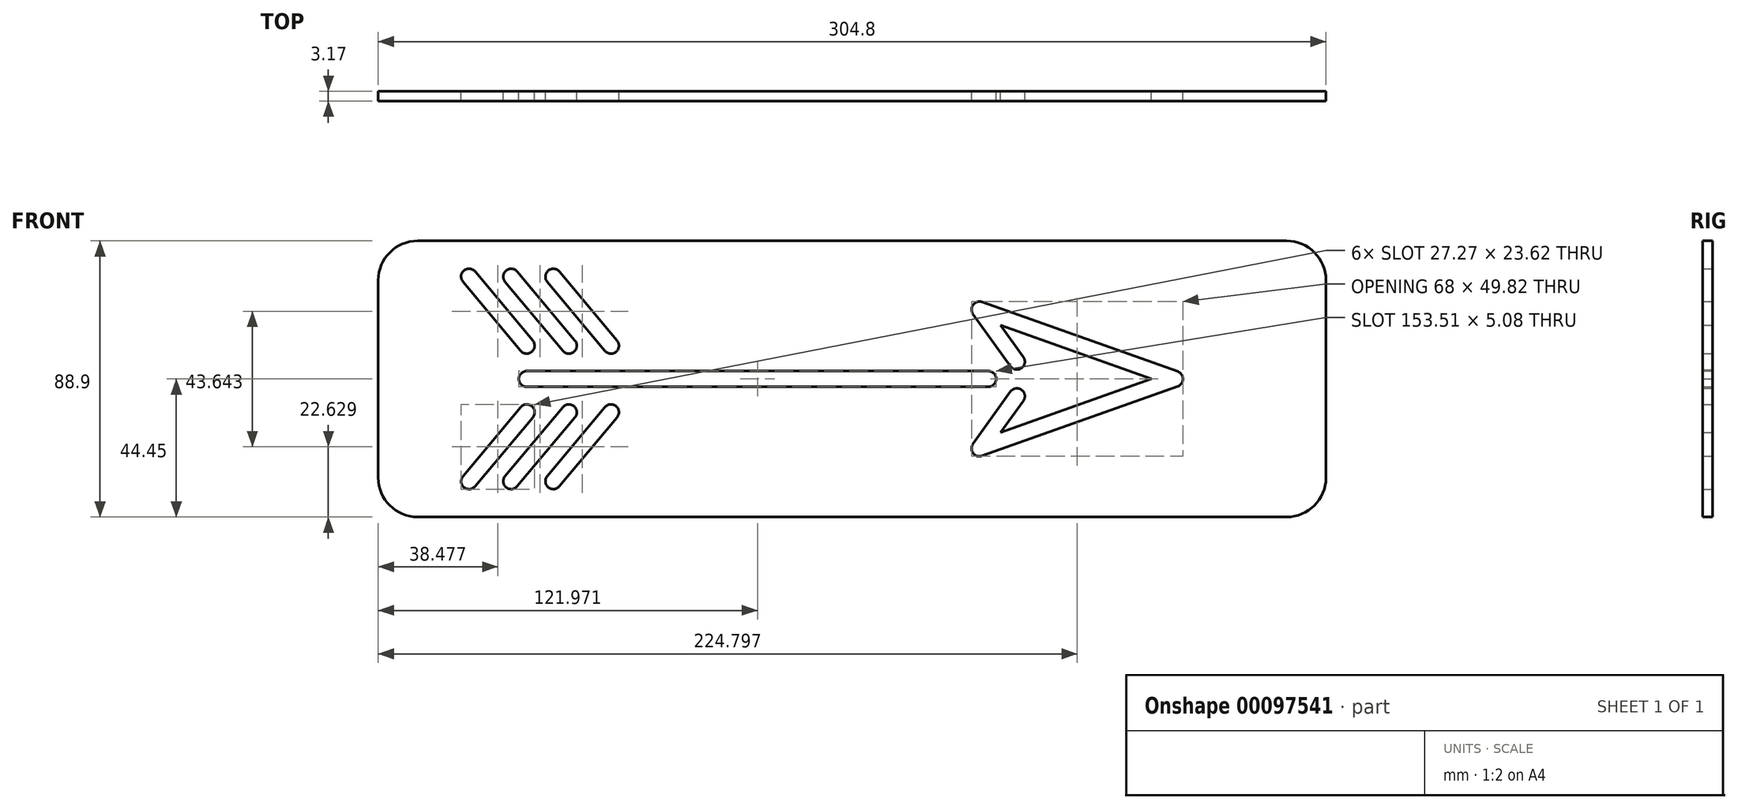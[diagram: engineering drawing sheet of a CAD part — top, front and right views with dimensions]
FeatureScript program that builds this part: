
annotation { "Feature Type Name" : "Feature", "Feature Type Description" : "" }
export const myFeature = defineFeature(function(context is Context, id is Id, definition is map)
    precondition{}
    {
        {
            var Q0;
            Q0=qCreatedBy(makeId("Front.planeOp"),FACE);
            var sketch = newSketch(context, id + "F0", { "sketchPlane" : qUnion([Q0])});
            skLineSegment(sketch, "E0.bottom", {"start": v(-139.7, -44.45) * mm, "end": v(139.7, -44.45) * mm});
            skLineSegment(sketch, "E0.top", {"start": v(-139.7, 44.45) * mm, "end": v(139.7, 44.45) * mm});
            skLineSegment(sketch, "E0.left", {"start": v(-152.4, -31.75) * mm, "end": v(-152.4, 31.75) * mm});
            skLineSegment(sketch, "E0.right", {"start": v(152.4, -31.75) * mm, "end": v(152.4, 31.75) * mm});
            skPoint(sketch, "E0.middle", {"position": v(0, 0) * mm});
            skArc(sketch, "E1.1.startCap", {"start": v(-75.59, 12.34) * mm, "mid": v(-75.91, 8.77) * mm, "end": v(-79.49, 9.09) * mm});
            skArc(sketch, "E1.1.endCap", {"start": v(-98.05, 31.3) * mm, "mid": v(-97.73, 34.88) * mm, "end": v(-94.15, 34.56) * mm});
            skLineSegment(sketch, "E1.1.left", {"start": v(-79.49, 9.09) * mm, "end": v(-98.05, 31.3) * mm});
            skLineSegment(sketch, "E1.1.right", {"start": v(-75.59, 12.34) * mm, "end": v(-94.15, 34.56) * mm});
            skArc(sketch, "E1.2.startCap", {"start": v(-89.14, 12.34) * mm, "mid": v(-89.46, 8.77) * mm, "end": v(-93.04, 9.09) * mm});
            skArc(sketch, "E1.2.endCap", {"start": v(-111.6, 31.3) * mm, "mid": v(-111.28, 34.88) * mm, "end": v(-107.7, 34.56) * mm});
            skLineSegment(sketch, "E1.2.left", {"start": v(-93.04, 9.09) * mm, "end": v(-111.6, 31.3) * mm});
            skLineSegment(sketch, "E1.2.right", {"start": v(-89.14, 12.34) * mm, "end": v(-107.7, 34.56) * mm});
            skArc(sketch, "E1.3.startCap", {"start": v(-102.7, 12.34) * mm, "mid": v(-103.01, 8.77) * mm, "end": v(-106.6, 9.09) * mm});
            skArc(sketch, "E1.3.endCap", {"start": v(-125.15, 31.3) * mm, "mid": v(-124.83, 34.88) * mm, "end": v(-121.26, 34.56) * mm});
            skLineSegment(sketch, "E1.3.left", {"start": v(-106.6, 9.09) * mm, "end": v(-125.15, 31.3) * mm});
            skLineSegment(sketch, "E1.3.right", {"start": v(-102.7, 12.34) * mm, "end": v(-121.26, 34.56) * mm});
            skArc(sketch, "E2.0.startCap", {"start": v(-104.64, -2.54) * mm, "mid": v(-107.18, 0) * mm, "end": v(-104.64, 2.54) * mm});
            skArc(sketch, "E2.0.endCap", {"start": v(43.78, 2.54) * mm, "mid": v(46.32, 0) * mm, "end": v(43.78, -2.54) * mm});
            skLineSegment(sketch, "E2.0.left", {"start": v(-104.64, 2.54) * mm, "end": v(43.78, 2.54) * mm});
            skLineSegment(sketch, "E2.0.right", {"start": v(-104.64, -2.54) * mm, "end": v(43.78, -2.54) * mm});
            skLineSegment(sketch, "E3", {"start": v(-104.64, 10.71) * mm, "end": v(-91.1, 10.71) * mm, "construction": true});
            skLineSegment(sketch, "E4", {"start": v(-91.1, 10.71) * mm, "end": v(-77.54, 10.71) * mm, "construction": true});
            skLineSegment(sketch, "E5", {"start": v(-77.54, 10.71) * mm, "end": v(-75, 10.71) * mm, "construction": true});
            skPoint(sketch, "E6.visualSharp", {"position": v(-152.4, 44.45) * mm});
            skArc(sketch, "E6.filletArc", {"start": v(-139.7, 44.45) * mm, "mid": v(-148.68, 40.73) * mm, "end": v(-152.4, 31.75) * mm});
            skPoint(sketch, "E7.visualSharp", {"position": v(-152.4, -44.45) * mm});
            skArc(sketch, "E7.filletArc", {"start": v(-152.4, -31.75) * mm, "mid": v(-148.68, -40.73) * mm, "end": v(-139.7, -44.45) * mm});
            skPoint(sketch, "E8.visualSharp", {"position": v(152.4, 44.45) * mm});
            skArc(sketch, "E8.filletArc", {"start": v(152.4, 31.75) * mm, "mid": v(148.68, 40.73) * mm, "end": v(139.7, 44.45) * mm});
            skPoint(sketch, "E9.visualSharp", {"position": v(152.4, -44.45) * mm});
            skArc(sketch, "E9.filletArc", {"start": v(139.7, -44.45) * mm, "mid": v(148.68, -40.73) * mm, "end": v(152.4, -31.75) * mm});
            skArc(sketch, "E10.MirrorCS", {"start": v(-75.59, -12.34) * mm, "mid": v(-75.91, -8.77) * mm, "end": v(-79.49, -9.09) * mm});
            skArc(sketch, "E11.MirrorCS", {"start": v(-89.14, -12.34) * mm, "mid": v(-89.46, -8.77) * mm, "end": v(-93.04, -9.09) * mm});
            skArc(sketch, "E12.MirrorCS", {"start": v(-102.7, -12.34) * mm, "mid": v(-103.01, -8.77) * mm, "end": v(-106.6, -9.09) * mm});
            skArc(sketch, "E13.MirrorCS", {"start": v(-111.6, -31.3) * mm, "mid": v(-111.28, -34.88) * mm, "end": v(-107.7, -34.56) * mm});
            skArc(sketch, "E14.MirrorCS", {"start": v(-125.15, -31.3) * mm, "mid": v(-124.83, -34.88) * mm, "end": v(-121.26, -34.56) * mm});
            skArc(sketch, "E15.MirrorCS", {"start": v(-98.05, -31.3) * mm, "mid": v(-97.73, -34.88) * mm, "end": v(-94.15, -34.56) * mm});
            skLineSegment(sketch, "E16.MirrorCS", {"start": v(-106.6, -9.09) * mm, "end": v(-125.15, -31.3) * mm});
            skLineSegment(sketch, "E17.MirrorCS", {"start": v(-102.7, -12.34) * mm, "end": v(-121.26, -34.56) * mm});
            skLineSegment(sketch, "E18.MirrorCS", {"start": v(-93.04, -9.09) * mm, "end": v(-111.6, -31.3) * mm});
            skLineSegment(sketch, "E19.MirrorCS", {"start": v(-89.14, -12.34) * mm, "end": v(-107.7, -34.56) * mm});
            skLineSegment(sketch, "E20.MirrorCS", {"start": v(-79.49, -9.09) * mm, "end": v(-98.05, -31.3) * mm});
            skLineSegment(sketch, "E21.MirrorCS", {"start": v(-75.59, -12.34) * mm, "end": v(-94.15, -34.56) * mm});
            skArc(sketch, "E22.0.startCap", {"start": v(55.07, 7.05) * mm, "mid": v(54.49, 3.5) * mm, "end": v(50.94, 4.08) * mm});
            skArc(sketch, "E22.0.endCap", {"start": v(38.88, 20.89) * mm, "mid": v(38.9, 23.9) * mm, "end": v(41.79, 24.76) * mm});
            skLineSegment(sketch, "E22.0.left", {"start": v(50.94, 4.08) * mm, "end": v(38.88, 20.89) * mm});
            skLineSegment(sketch, "E22.0.right", {"start": v(55.07, 7.05) * mm, "end": v(47.74, 17.26) * mm});
            skArc(sketch, "E22.1.startCap", {"start": v(38.88, 20.89) * mm, "mid": v(38.9, 23.9) * mm, "end": v(41.79, 24.76) * mm});
            skArc(sketch, "E22.1.endCap", {"start": v(104.7, 2.4) * mm, "mid": v(106.4, 0) * mm, "end": v(104.7, -2.4) * mm});
            skLineSegment(sketch, "E22.1.left", {"start": v(41.79, 24.76) * mm, "end": v(104.7, 2.4) * mm});
            skArc(sketch, "E23.MirrorCS", {"start": v(38.88, -20.89) * mm, "mid": v(38.9, -23.9) * mm, "end": v(41.79, -24.76) * mm});
            skLineSegment(sketch, "E24.MirrorCS", {"start": v(50.94, -4.08) * mm, "end": v(38.88, -20.89) * mm});
            skLineSegment(sketch, "E25.MirrorCS", {"start": v(55.07, -7.05) * mm, "end": v(47.74, -17.26) * mm});
            skLineSegment(sketch, "E26.MirrorCS", {"start": v(41.79, -24.76) * mm, "end": v(104.7, -2.4) * mm});
            skLineSegment(sketch, "E27.MirrorCS", {"start": v(47.74, -17.26) * mm, "end": v(96.27, 0) * mm});
            skArc(sketch, "E28.MirrorCS", {"start": v(55.07, -7.05) * mm, "mid": v(54.49, -3.5) * mm, "end": v(50.94, -4.08) * mm});
            skPoint(sketch, "E29.orphan", {"position": v(40.09, -19.98) * mm});
            skLineSegment(sketch, "E30.trimOffspring", {"start": v(47.74, 17.26) * mm, "end": v(96.27, 0) * mm});
            skPoint(sketch, "E31.orphan", {"position": v(40.09, 19.98) * mm});
            skPoint(sketch, "E32.orphan", {"position": v(43, 23.85) * mm});
            skPoint(sketch, "E33.orphan", {"position": v(103, 2.4) * mm});
            skPoint(sketch, "E34.orphan", {"position": v(103, -2.4) * mm});
            skPoint(sketch, "E35.orphan", {"position": v(43, -23.85) * mm});
            skPoint(sketch, "E36.orphan", {"position": v(-63.99, 10.71) * mm});
            skSolve(sketch);
        }
        {
            var Q0;
            Q0 = qSketchRegion(id + "F0", true);
            extrude(context, id + "F1", {"entities" : qUnion([Q0]), "depth" : 3.17 * mm});
        }
    });
